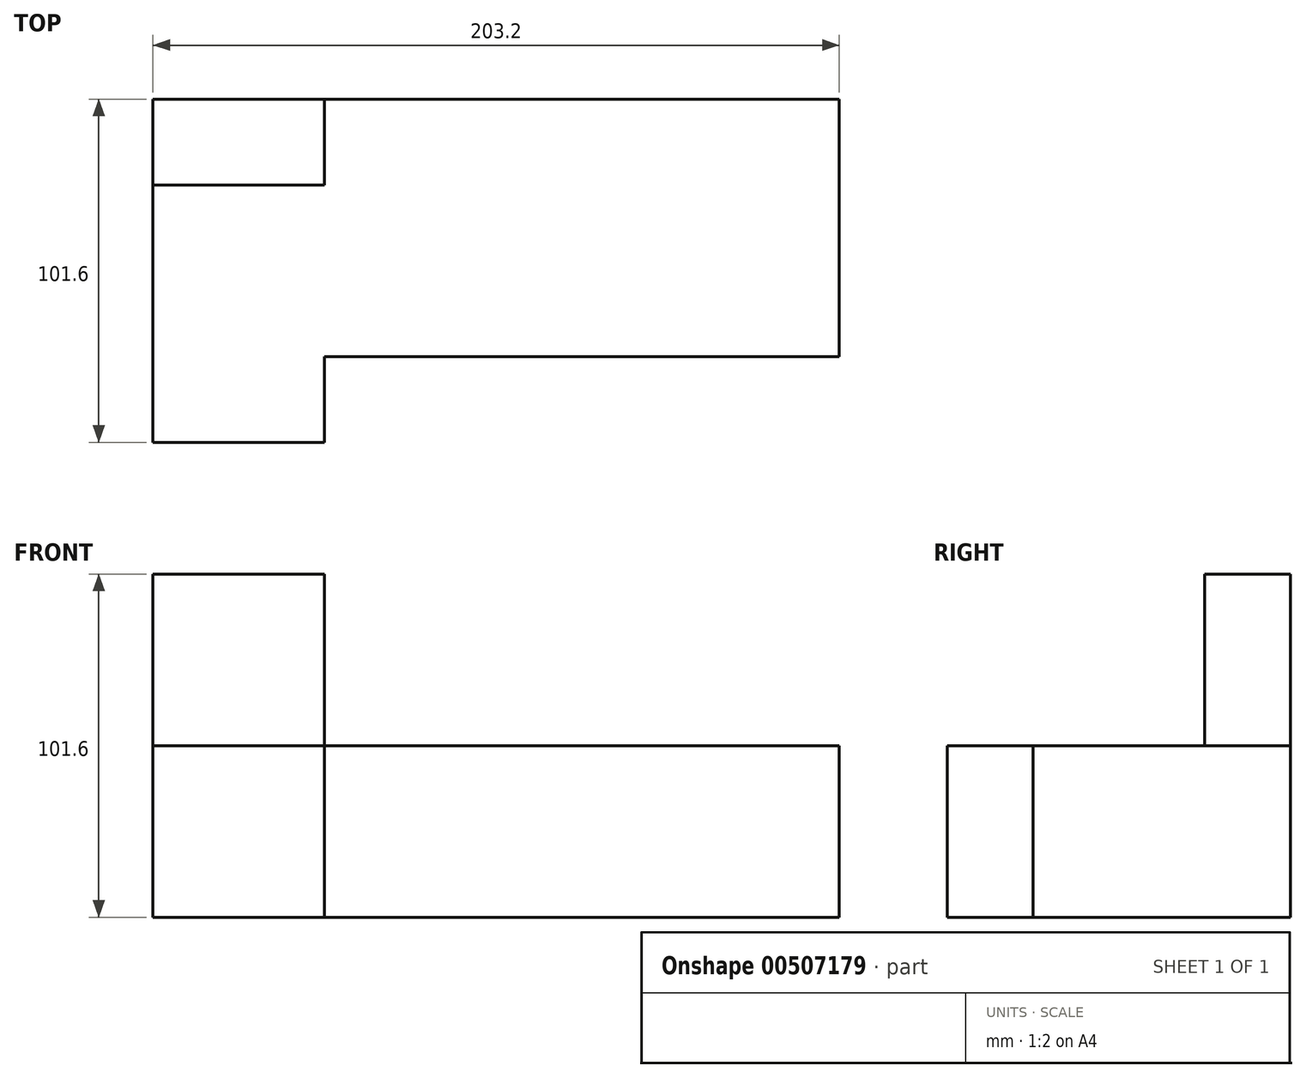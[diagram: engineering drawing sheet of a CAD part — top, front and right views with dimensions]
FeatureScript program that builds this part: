
annotation { "Feature Type Name" : "Feature", "Feature Type Description" : "" }
export const myFeature = defineFeature(function(context is Context, id is Id, definition is map)
    precondition{}
    {
        {
            var Q0;
            Q0=qCreatedBy(makeId("Top.planeOp"),FACE);
            var sketch = newSketch(context, id + "F0", { "sketchPlane" : qUnion([Q0])});
            skLineSegment(sketch, "E0.bottom", {"start": v(0, 0) * mm, "end": v(203.2, 0) * mm});
            skLineSegment(sketch, "E0.top", {"start": v(0, -101.6) * mm, "end": v(203.2, -101.6) * mm});
            skLineSegment(sketch, "E0.left", {"start": v(0, 0) * mm, "end": v(0, -101.6) * mm});
            skLineSegment(sketch, "E0.right", {"start": v(203.2, 0) * mm, "end": v(203.2, -101.6) * mm});
            skSolve(sketch);
        }
        {
            var Q0;
            Q0=makeQuery(id+"F0.imprint","IMPRINT",FACE,{"disambiguationData":[TD([[makeQuery(id+"F0.imprint","IMPRINT",EDGE,{"derivedFrom":sQuery(id+"F0.wireOp",EDGE,"E0.bottom")}),-1.0]])]});
            extrude(context, id + "F1", {"entities" : qUnion([Q0]), "depth" : 50.8 * mm});
        }
        {
            var Q0;
            Q0=makeQuery(id+"F1.opExtrude","SWEPT_FACE",FACE,{"disambiguationData":[OSD([sQuery(id+"F0.wireOp",EDGE,"E0.right")])]});
            var sketch = newSketch(context, id + "F2", { "sketchPlane" : qUnion([Q0])});
            skLineSegment(sketch, "E1", {"start": v(-101.6, 0) * mm, "end": v(-101.6, 50.8) * mm});
            skLineSegment(sketch, "E2", {"start": v(-101.6, 50.8) * mm, "end": v(-76.2, 50.8) * mm});
            skLineSegment(sketch, "E3", {"start": v(-76.2, 50.8) * mm, "end": v(-76.2, 0) * mm});
            skLineSegment(sketch, "E4", {"start": v(-76.2, 0) * mm, "end": v(-101.6, 0) * mm});
            skSolve(sketch);
        }
        {
            var Q0;
            Q0=makeQuery(id+"F2.imprint","IMPRINT",FACE,{"disambiguationData":[TD([[makeQuery(id+"F2.imprint","IMPRINT",EDGE,{"derivedFrom":sQuery(id+"F2.wireOp",EDGE,"E1")}),1.0]])]});
            extrude(context, id + "F3", {"entities" : qUnion([Q0]), "operationType" : NewBodyOperationType.REMOVE, "oppositeDirection" : true, "depth" : 152.4 * mm});
        }
        {
            var Q0;
            Q0=makeQuery(id+"F1.opExtrude","CAP_FACE",FACE,{"disambiguationData":[OSD([sQuery(id+"F0.wireOp",EDGE,"E0.bottom"),sQuery(id+"F0.wireOp",EDGE,"E0.top"),sQuery(id+"F0.wireOp",EDGE,"E0.left"),sQuery(id+"F0.wireOp",EDGE,"E0.right")])],"isStart":false});
            var sketch = newSketch(context, id + "F4", { "sketchPlane" : qUnion([Q0])});
            skLineSegment(sketch, "E5.bottom", {"start": v(0, 0) * mm, "end": v(50.8, 0) * mm});
            skLineSegment(sketch, "E5.top", {"start": v(0, -25.4) * mm, "end": v(50.8, -25.4) * mm});
            skLineSegment(sketch, "E5.left", {"start": v(0, 0) * mm, "end": v(0, -25.4) * mm});
            skLineSegment(sketch, "E5.right", {"start": v(50.8, 0) * mm, "end": v(50.8, -25.4) * mm});
            skSolve(sketch);
        }
        {
            var Q0;
            Q0=makeQuery(id+"F4.imprint","IMPRINT",FACE,{"disambiguationData":[TD([[makeQuery(id+"F4.imprint","IMPRINT",EDGE,{"derivedFrom":sQuery(id+"F4.wireOp",EDGE,"E5.bottom")}),-1.0]])]});
            extrude(context, id + "F5", {"entities" : qUnion([Q0]), "operationType" : NewBodyOperationType.ADD, "depth" : 50.8 * mm});
        }
    });
